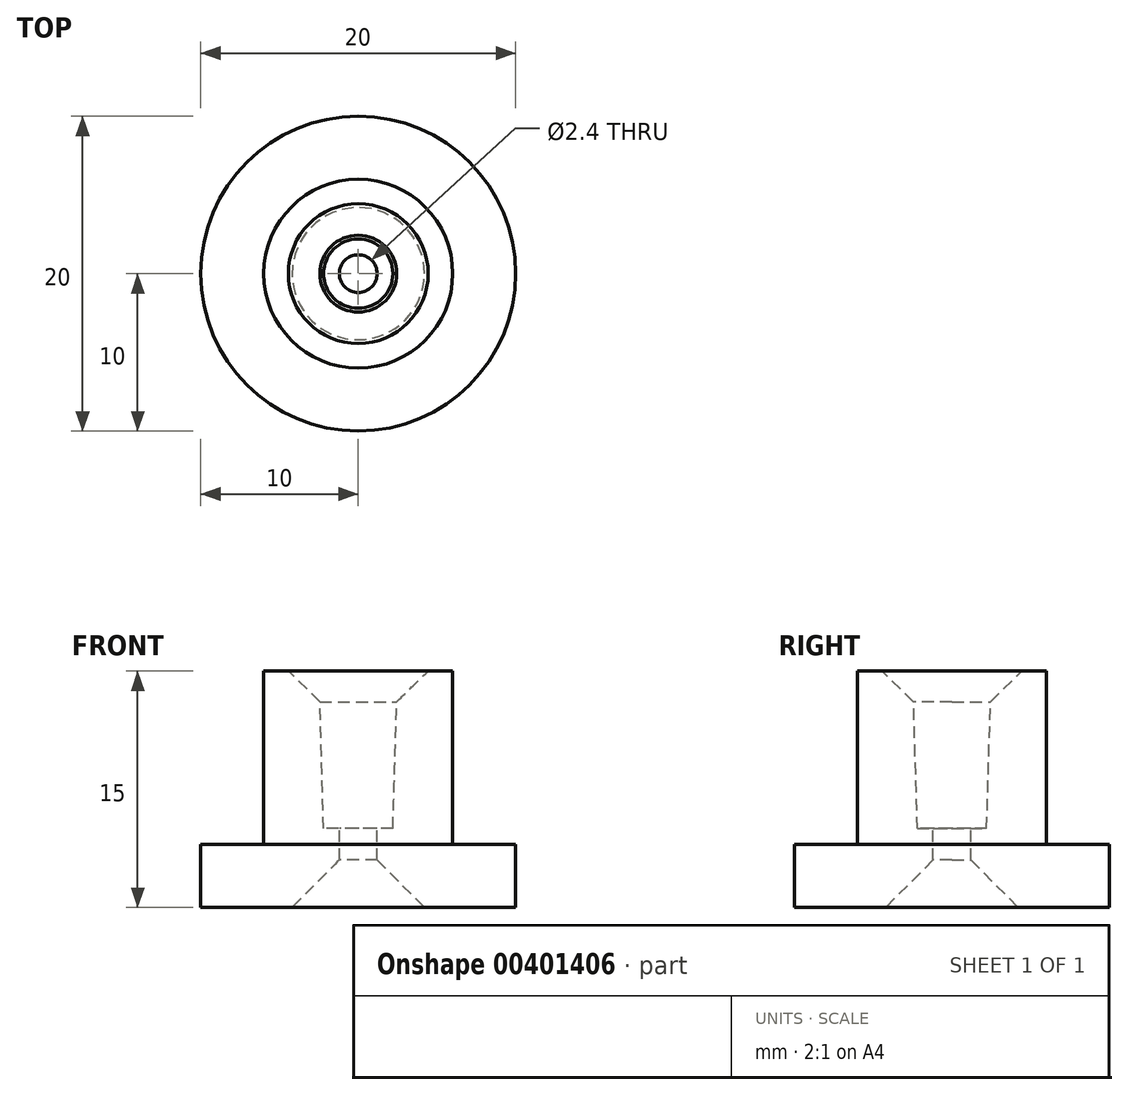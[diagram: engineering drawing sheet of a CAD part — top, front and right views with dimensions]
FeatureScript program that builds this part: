
annotation { "Feature Type Name" : "Feature", "Feature Type Description" : "" }
export const myFeature = defineFeature(function(context is Context, id is Id, definition is map)
    precondition{}
    {
        {
            var Q0;
            Q0=qCreatedBy(makeId("Front.planeOp"),FACE);
            var sketch = newSketch(context, id + "F0", { "sketchPlane" : qUnion([Q0])});
            skLineSegment(sketch, "E0", {"start": v(-1.2, 5) * mm, "end": v(-2.2, 5) * mm});
            skLineSegment(sketch, "E1", {"start": v(-6, 15) * mm, "end": v(-6, 4) * mm});
            skLineSegment(sketch, "E2", {"start": v(-6, 4) * mm, "end": v(-10, 4) * mm});
            skLineSegment(sketch, "E3", {"start": v(0, 12.14) * mm, "end": v(0, -4.82) * mm, "construction": true});
            skLineSegment(sketch, "E4", {"start": v(-10, 4) * mm, "end": v(-10, 0) * mm});
            skLineSegment(sketch, "E5", {"start": v(-10, 0) * mm, "end": v(-1.2, 0) * mm});
            skLineSegment(sketch, "E6", {"start": v(-1.2, 0) * mm, "end": v(-1.2, 5) * mm});
            skLineSegment(sketch, "E7", {"start": v(-2.2, 5) * mm, "end": v(-2.5, 15) * mm});
            skLineSegment(sketch, "E8", {"start": v(-2.5, 15) * mm, "end": v(-6, 15) * mm});
            skSolve(sketch);
        }
        {
            var Q0;
            Q0=makeQuery(id+"F0.imprint","IMPRINT",FACE,{"disambiguationData":[TD([[makeQuery(id+"F0.imprint","IMPRINT",EDGE,{"derivedFrom":sQuery(id+"F0.wireOp",EDGE,"E0")}),1.0]])]});
            var Q1;
            Q1=sQuery(id+"F0.wireOp",EDGE,"E3");
            revolve(context, id + "F1", {"entities" : qUnion([Q0]), "axis" : qUnion([Q1]), "revolveType" : RevolveType.FULL});
        }
        {
            var Q0;
            Q0=makeQuery(id+"F1.opRevolve","SWEPT_EDGE",EDGE,{"disambiguationData":[OSD([sQuery(id+"F0.wireOp",EDGE,"E5"),sQuery(id+"F0.wireOp",EDGE,"E6")])]});
            chamfer(context, id + "F2", {"entities" : qUnion([Q0]), "width" : 3 * mm, "tangentPropagation" : true});
        }
        {
            var Q0;
            Q0=makeQuery(id+"F1.opRevolve","SWEPT_EDGE",EDGE,{"disambiguationData":[OSD([sQuery(id+"F0.wireOp",EDGE,"E7"),sQuery(id+"F0.wireOp",EDGE,"E8")])]});
            chamfer(context, id + "F3", {"entities" : qUnion([Q0]), "width" : 2 * mm, "tangentPropagation" : true});
        }
    });
